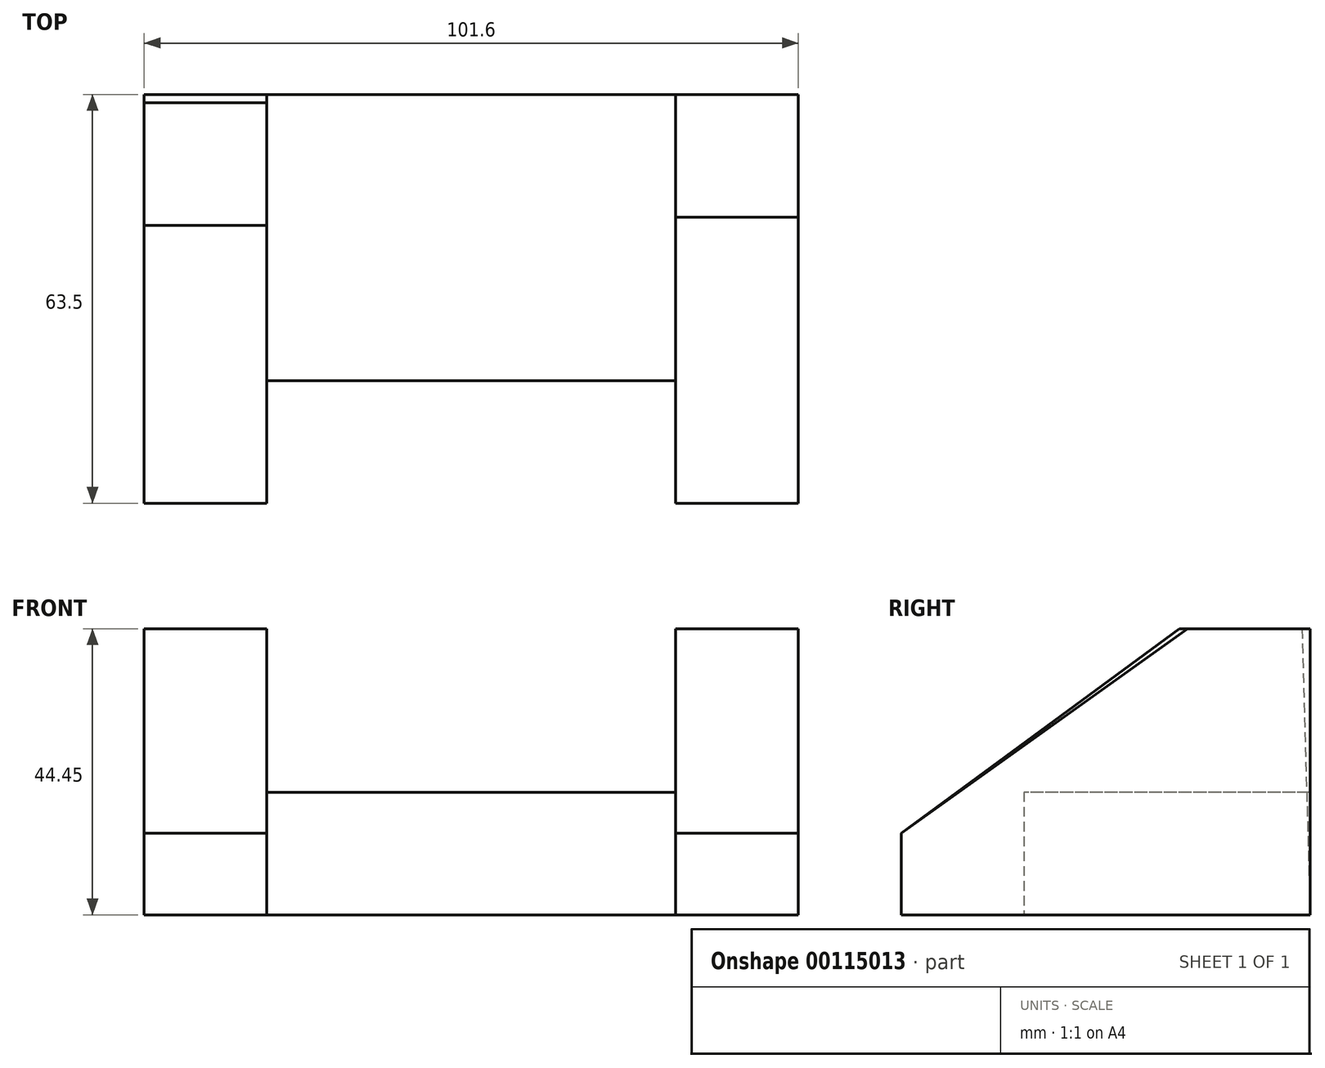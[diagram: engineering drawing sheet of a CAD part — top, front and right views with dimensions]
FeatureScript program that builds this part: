
annotation { "Feature Type Name" : "Feature", "Feature Type Description" : "" }
export const myFeature = defineFeature(function(context is Context, id is Id, definition is map)
    precondition{}
    {
        {
            var Q0;
            Q0=qCreatedBy(makeId("Right.planeOp"),FACE);
            var sketch = newSketch(context, id + "F0", { "sketchPlane" : qUnion([Q0])});
            skLineSegment(sketch, "E0", {"start": v(-4.07, 21.37) * mm, "end": v(14.98, 21.37) * mm});
            skLineSegment(sketch, "E1", {"start": v(14.98, 21.37) * mm, "end": v(14.98, -23.08) * mm});
            skLineSegment(sketch, "E2", {"start": v(14.98, -23.08) * mm, "end": v(-48.52, -23.08) * mm});
            skLineSegment(sketch, "E3", {"start": v(-48.52, -23.08) * mm, "end": v(-48.52, -10.38) * mm});
            skLineSegment(sketch, "E4", {"start": v(-48.52, -10.38) * mm, "end": v(-4.07, 21.37) * mm});
            skSolve(sketch);
        }
        {
            var Q0;
            Q0 = qSketchRegion(id + "F0", true);
            extrude(context, id + "F1", {"entities" : qUnion([Q0]), "depth" : 19.05 * mm});
        }
        {
            var Q0;
            Q0=makeQuery(id+"F1.opExtrude","CAP_FACE",FACE,{"disambiguationData":[OSD([sQuery(id+"F0.wireOp",EDGE,"E0"),sQuery(id+"F0.wireOp",EDGE,"E1"),sQuery(id+"F0.wireOp",EDGE,"E2"),sQuery(id+"F0.wireOp",EDGE,"E3"),sQuery(id+"F0.wireOp",EDGE,"E4")])],"isStart":true});
            var sketch = newSketch(context, id + "F2", { "sketchPlane" : qUnion([Q0])});
            skLineSegment(sketch, "E5", {"start": v(-14.98, -4.03) * mm, "end": v(29.47, -4.03) * mm});
            skLineSegment(sketch, "E6", {"start": v(29.47, -4.03) * mm, "end": v(29.47, -23.08) * mm});
            skLineSegment(sketch, "E7", {"start": v(29.47, -23.08) * mm, "end": v(-14.98, -23.08) * mm});
            skLineSegment(sketch, "E8", {"start": v(-14.98, -23.08) * mm, "end": v(-14.98, -4.03) * mm});
            skSolve(sketch);
        }
        {
            var Q0;
            Q0 = qSketchRegion(id + "F2", true);
            extrude(context, id + "F3", {"entities" : qUnion([Q0]), "operationType" : NewBodyOperationType.ADD, "depth" : 63.5 * mm});
        }
        {
            var Q0;
            Q0=makeQuery(id+"F3.opExtrude","CAP_FACE",FACE,{"disambiguationData":[OSD([sQuery(id+"F2.wireOp",EDGE,"E5"),sQuery(id+"F2.wireOp",EDGE,"E6"),sQuery(id+"F2.wireOp",EDGE,"E7"),sQuery(id+"F2.wireOp",EDGE,"E8")])],"isStart":false});
            var sketch = newSketch(context, id + "F4", { "sketchPlane" : qUnion([Q0])});
            skLineSegment(sketch, "E9", {"start": v(-14.98, -23.08) * mm, "end": v(48.52, -23.08) * mm});
            skPoint(sketch, "E9.endSnap0", {"position": v(7.25, -23.08) * mm});
            skLineSegment(sketch, "E10", {"start": v(48.52, -23.08) * mm, "end": v(48.52, -10.38) * mm});
            skLineSegment(sketch, "E11", {"start": v(48.52, -10.38) * mm, "end": v(5.35, 21.35) * mm});
            skLineSegment(sketch, "E12", {"start": v(5.35, 21.35) * mm, "end": v(-13.7, 21.35) * mm});
            skLineSegment(sketch, "E13", {"start": v(-13.7, 21.35) * mm, "end": v(-14.98, -23.08) * mm});
            skSolve(sketch);
        }
        {
            var Q0;
            Q0 = qSketchRegion(id + "F4", true);
            extrude(context, id + "F5", {"entities" : qUnion([Q0]), "operationType" : NewBodyOperationType.ADD, "depth" : 19.05 * mm});
        }
    });
